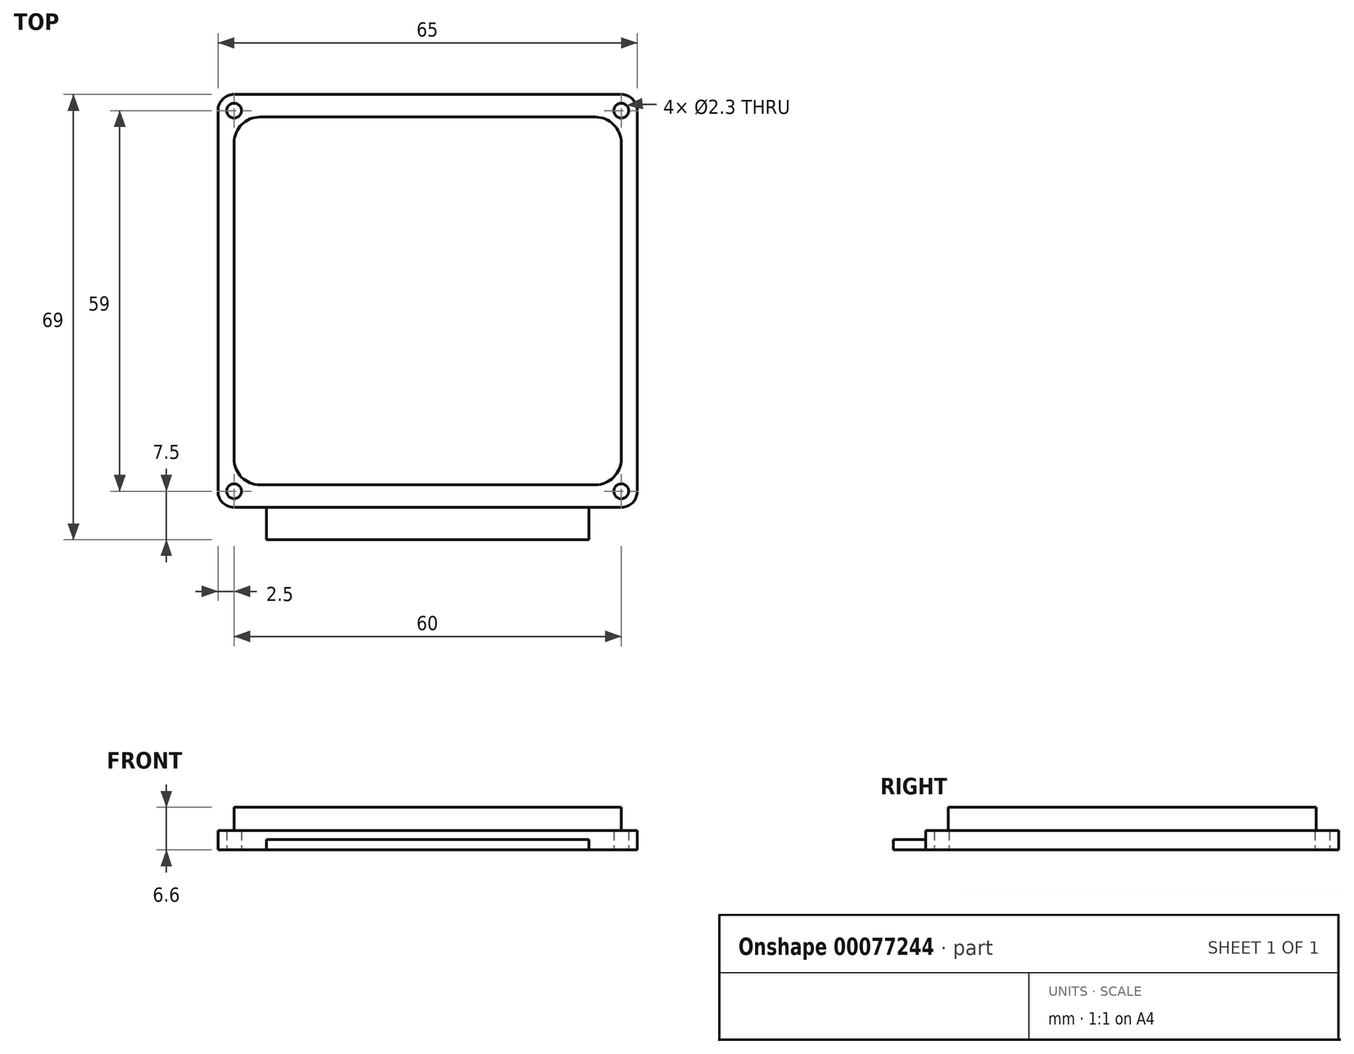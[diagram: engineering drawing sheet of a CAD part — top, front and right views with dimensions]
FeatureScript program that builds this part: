
annotation { "Feature Type Name" : "Feature", "Feature Type Description" : "" }
export const myFeature = defineFeature(function(context is Context, id is Id, definition is map)
    precondition{}
    {
        {
            var Q0;
            Q0=qCreatedBy(makeId("Top.planeOp"),FACE);
            var sketch = newSketch(context, id + "F0", { "sketchPlane" : qUnion([Q0])});
            skLineSegment(sketch, "E0.bottom", {"start": v(-30, -32) * mm, "end": v(30, -32) * mm});
            skLineSegment(sketch, "E0.top", {"start": v(-30, 32) * mm, "end": v(30, 32) * mm});
            skLineSegment(sketch, "E0.left", {"start": v(-32.5, -29.5) * mm, "end": v(-32.5, 29.5) * mm});
            skLineSegment(sketch, "E0.right", {"start": v(32.5, -29.5) * mm, "end": v(32.5, 29.5) * mm});
            skCircle(sketch, "E1", {"center": v(-30, 29.5) * mm, "radius": 1.15 * mm});
            skCircle(sketch, "E2", {"center": v(-30, -29.5) * mm, "radius": 1.15 * mm});
            skCircle(sketch, "E3", {"center": v(30, -29.5) * mm, "radius": 1.15 * mm});
            skCircle(sketch, "E4", {"center": v(30, 29.5) * mm, "radius": 1.15 * mm});
            skPoint(sketch, "E5.visualSharp", {"position": v(-32.5, 32) * mm});
            skArc(sketch, "E5.filletArc", {"start": v(-30, 32) * mm, "mid": v(-31.77, 31.27) * mm, "end": v(-32.5, 29.5) * mm});
            skPoint(sketch, "E6.visualSharp", {"position": v(-32.5, -32) * mm});
            skArc(sketch, "E6.filletArc", {"start": v(-32.5, -29.5) * mm, "mid": v(-31.77, -31.27) * mm, "end": v(-30, -32) * mm});
            skPoint(sketch, "E7.visualSharp", {"position": v(32.5, -32) * mm});
            skArc(sketch, "E7.filletArc", {"start": v(30, -32) * mm, "mid": v(31.77, -31.27) * mm, "end": v(32.5, -29.5) * mm});
            skPoint(sketch, "E8.visualSharp", {"position": v(32.5, 32) * mm});
            skArc(sketch, "E8.filletArc", {"start": v(32.5, 29.5) * mm, "mid": v(31.77, 31.27) * mm, "end": v(30, 32) * mm});
            skLineSegment(sketch, "E9", {"start": v(-30, 29.5) * mm, "end": v(30, 29.5) * mm, "construction": true});
            skLineSegment(sketch, "E10", {"start": v(30, -29.5) * mm, "end": v(30, 29.5) * mm, "construction": true});
            skLineSegment(sketch, "E11", {"start": v(30, -29.5) * mm, "end": v(-30, -29.5) * mm, "construction": true});
            skLineSegment(sketch, "E12", {"start": v(-30, -29.5) * mm, "end": v(-30, 29.5) * mm, "construction": true});
            skLineSegment(sketch, "E13", {"start": v(0, 29.5) * mm, "end": v(0, 32) * mm, "construction": true});
            skLineSegment(sketch, "E14", {"start": v(-30, 0) * mm, "end": v(-32.5, 0) * mm, "construction": true});
            skLineSegment(sketch, "E15", {"start": v(-30, 29.5) * mm, "end": v(30, -29.5) * mm, "construction": true});
            skSolve(sketch);
        }
        {
            var Q0;
            Q0=makeQuery(id+"F0.imprint","IMPRINT",FACE,{"disambiguationData":[TD([[makeQuery(id+"F0.imprint","IMPRINT",EDGE,{"derivedFrom":sQuery(id+"F0.wireOp",EDGE,"E0.bottom")}),1.0]])]});
            extrude(context, id + "F1", {"entities" : qUnion([Q0]), "depth" : 3 * mm});
        }
        {
            var Q0;
            Q0=makeQuery(id+"F1.opExtrude","CAP_FACE",FACE,{"disambiguationData":[OSD([sQuery(id+"F0.wireOp",EDGE,"E0.bottom"),sQuery(id+"F0.wireOp",EDGE,"E0.top"),sQuery(id+"F0.wireOp",EDGE,"E0.left"),sQuery(id+"F0.wireOp",EDGE,"E0.right"),sQuery(id+"F0.wireOp",EDGE,"E1"),sQuery(id+"F0.wireOp",EDGE,"E2"),sQuery(id+"F0.wireOp",EDGE,"E3"),sQuery(id+"F0.wireOp",EDGE,"E4"),sQuery(id+"F0.wireOp",EDGE,"E5.filletArc"),sQuery(id+"F0.wireOp",EDGE,"E6.filletArc"),sQuery(id+"F0.wireOp",EDGE,"E7.filletArc"),sQuery(id+"F0.wireOp",EDGE,"E8.filletArc")])],"isStart":false});
            var sketch = newSketch(context, id + "F2", { "sketchPlane" : qUnion([Q0])});
            skLineSegment(sketch, "E16.bottom", {"start": v(-26, 28.5) * mm, "end": v(26, 28.5) * mm});
            skLineSegment(sketch, "E16.top", {"start": v(-26, -28.5) * mm, "end": v(26, -28.5) * mm});
            skLineSegment(sketch, "E16.left", {"start": v(-30, 24.5) * mm, "end": v(-30, -24.5) * mm});
            skLineSegment(sketch, "E16.right", {"start": v(30, 24.5) * mm, "end": v(30, -24.5) * mm});
            skLineSegment(sketch, "E17", {"start": v(0, 28.5) * mm, "end": v(0, 32) * mm, "construction": true});
            skLineSegment(sketch, "E18", {"start": v(-30, 0) * mm, "end": v(-32.5, 0) * mm, "construction": true});
            skPoint(sketch, "E19.visualSharp", {"position": v(-30, 28.5) * mm});
            skArc(sketch, "E19.filletArc", {"start": v(-26, 28.5) * mm, "mid": v(-28.83, 27.33) * mm, "end": v(-30, 24.5) * mm});
            skPoint(sketch, "E20.visualSharp", {"position": v(-30, -28.5) * mm});
            skArc(sketch, "E20.filletArc", {"start": v(-30, -24.5) * mm, "mid": v(-28.83, -27.33) * mm, "end": v(-26, -28.5) * mm});
            skPoint(sketch, "E21.visualSharp", {"position": v(30, -28.5) * mm});
            skArc(sketch, "E21.filletArc", {"start": v(26, -28.5) * mm, "mid": v(28.83, -27.33) * mm, "end": v(30, -24.5) * mm});
            skPoint(sketch, "E22.visualSharp", {"position": v(30, 28.5) * mm});
            skArc(sketch, "E22.filletArc", {"start": v(30, 24.5) * mm, "mid": v(28.83, 27.33) * mm, "end": v(26, 28.5) * mm});
            skSolve(sketch);
        }
        {
            var Q0;
            Q0=qSketchRegion(id+"F2",true);
            extrude(context, id + "F3", {"entities" : qUnion([Q0]), "operationType" : NewBodyOperationType.ADD, "depth" : 3.6 * mm});
        }
        {
            var Q0;
            Q0=makeQuery(id+"F1.opExtrude","CAP_FACE",FACE,{"disambiguationData":[OSD([sQuery(id+"F0.wireOp",EDGE,"E0.bottom"),sQuery(id+"F0.wireOp",EDGE,"E0.top"),sQuery(id+"F0.wireOp",EDGE,"E0.left"),sQuery(id+"F0.wireOp",EDGE,"E0.right"),sQuery(id+"F0.wireOp",EDGE,"E1"),sQuery(id+"F0.wireOp",EDGE,"E2"),sQuery(id+"F0.wireOp",EDGE,"E3"),sQuery(id+"F0.wireOp",EDGE,"E4"),sQuery(id+"F0.wireOp",EDGE,"E5.filletArc"),sQuery(id+"F0.wireOp",EDGE,"E6.filletArc"),sQuery(id+"F0.wireOp",EDGE,"E7.filletArc"),sQuery(id+"F0.wireOp",EDGE,"E8.filletArc")])],"isStart":true});
            var sketch = newSketch(context, id + "F4", { "sketchPlane" : qUnion([Q0])});
            skLineSegment(sketch, "E23.bottom", {"start": v(-25, 37) * mm, "end": v(25, 37) * mm});
            skLineSegment(sketch, "E23.top", {"start": v(-25, 32) * mm, "end": v(25, 32) * mm});
            skLineSegment(sketch, "E23.left", {"start": v(-25, 37) * mm, "end": v(-25, 32) * mm});
            skLineSegment(sketch, "E23.right", {"start": v(25, 37) * mm, "end": v(25, 32) * mm});
            skLineSegment(sketch, "E24", {"start": v(0, 37) * mm, "end": v(0, -32) * mm});
            skSolve(sketch);
        }
        {
            var Q0;
            {var subQ0=sQuery(id+"F4.wireOp",EDGE,"E23.left");Q0=makeQuery(id+"F4.imprint","IMPRINT",FACE,{"disambiguationData":[TD([[makeQuery(id+"F4.imprint","IMPRINT",EDGE,{"derivedFrom":subQ0}),1.0]])]});}
            var Q1;
            {var subQ0=sQuery(id+"F4.wireOp",EDGE,"E23.right");Q1=makeQuery(id+"F4.imprint","IMPRINT",FACE,{"disambiguationData":[TD([[makeQuery(id+"F4.imprint","IMPRINT",EDGE,{"derivedFrom":subQ0}),-1.0]])]});}
            extrude(context, id + "F5", {"entities" : qUnion([Q0, Q1]), "operationType" : NewBodyOperationType.ADD, "oppositeDirection" : true, "depth" : 1.6 * mm});
        }
    });
